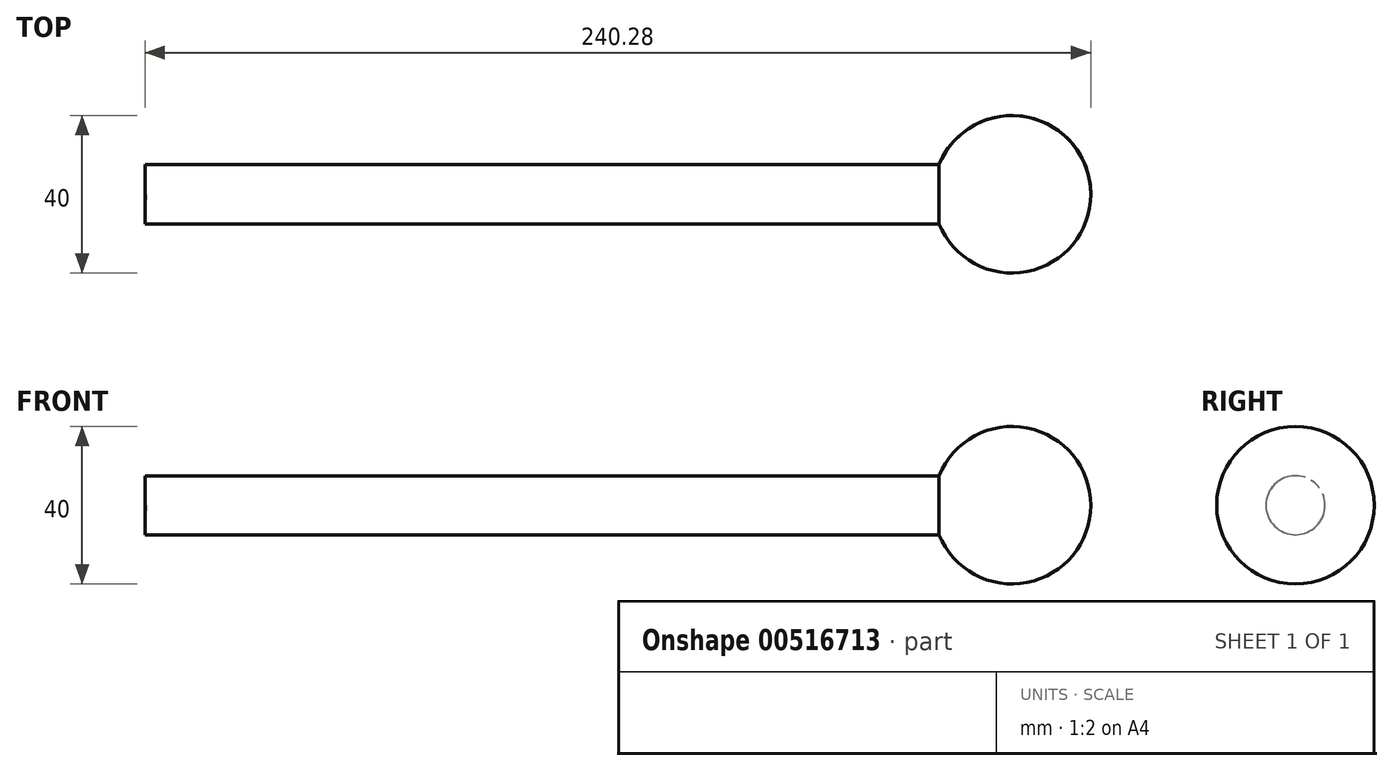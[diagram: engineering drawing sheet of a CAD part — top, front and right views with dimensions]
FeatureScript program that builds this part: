
annotation { "Feature Type Name" : "Feature", "Feature Type Description" : "" }
export const myFeature = defineFeature(function(context is Context, id is Id, definition is map)
    precondition{}
    {
        {
            var Q0;
            Q0=qCreatedBy(makeId("Top.planeOp"),FACE);
            var sketch = newSketch(context, id + "F0", { "sketchPlane" : qUnion([Q0])});
            skPoint(sketch, "E0.right.start.orphan", {"position": v(98.15, 7.36) * mm});
            skPoint(sketch, "E1.orphan", {"position": v(98.15, -7.36) * mm});
            skPoint(sketch, "E2.orphan", {"position": v(24.54, -26.86) * mm});
            skLineSegment(sketch, "E3.bottom", {"start": v(1.46, 7.5) * mm, "end": v(-200.28, 7.5) * mm});
            skLineSegment(sketch, "E3.right", {"start": v(-200.28, 7.5) * mm, "end": v(-200, 0) * mm});
            skPoint(sketch, "E3.middle", {"position": v(0, 0) * mm});
            skArc(sketch, "E4", {"start": v(40, 0) * mm, "mid": v(23.82, 19.63) * mm, "end": v(1.46, 7.5) * mm});
            skLineSegment(sketch, "E5", {"start": v(-200, 0) * mm, "end": v(200, 0) * mm, "construction": true});
            skPoint(sketch, "E6.orphan", {"position": v(-199.72, -7.5) * mm});
            skPoint(sketch, "E7.orphan", {"position": v(199.72, 7.5) * mm});
            skPoint(sketch, "E3.left.end.orphan", {"position": v(200.28, -7.5) * mm});
            skLineSegment(sketch, "E8", {"start": v(-200, 0) * mm, "end": v(40, 0) * mm});
            skSolve(sketch);
        }
        {
            var Q0;
            Q0 = qSketchRegion(id + "F0", true);
            var Q1;
            Q1=sQuery(id+"F0.wireOp",EDGE,"E5");
            revolve(context, id + "F1", {"entities" : qUnion([Q0]), "axis" : qUnion([Q1]), "revolveType" : RevolveType.FULL});
        }
    });
